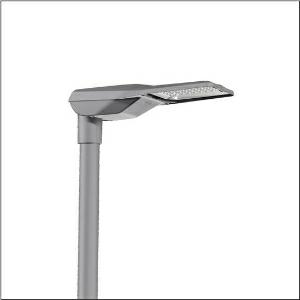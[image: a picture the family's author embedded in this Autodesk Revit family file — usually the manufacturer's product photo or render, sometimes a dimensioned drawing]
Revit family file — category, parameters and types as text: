
# Revit family: streetlight_sl_21_iq_mini___st0_5a_5xe2b31g08jb_3c5a
name_source: partatom
category: Lighting Fixtures
units: mm (PartAtom-declared; Revit-internal decimal feet)

## family parameters
Cut with Voids When Loaded = No
Host = Face
Light Source = No
Part Type = Normal
Room Calculation Point = No
Round Connector Dimension = Use Diameter
Shared = No

## types (1)
- --- (1 x LED, 10820 lm, 71.6 W, 3000K)
    Apparent Load = 72 VA
    CIE Flux Codes = 43 76 97 100 100
    Color Rendering = 70
    Color Temperature = 3000K
    Default Elevation = 1800 mm
    Description = Streetlight SL 21 mini, mast luminaire, primary light control with lens, of PMMA, primary optical cover: cover, of toughened safety glass, transparent, light distribution: ST0.5a, light emission: direct distribution, primary light characteristic: asymmetric, installation type: post-top, side-entry, LED, High Power LED, rated luminous flux: 10.820lm, luminous efficacy: 151lm/W, light colour: 730, colour temperature: 3000K, control gear: ECG iQ, control: Street-Remote, Auto-Match, Temp-Guard, Lumen-Switch, Night-Set, Smart-Wire, Light-Fading, Desk-Remote (wireless, voltage-free reading and setting of iQ features in the workshop via application-optimized NFC function/RFID function), optimised constant luminous flux control (CLO 2.0), mains connection: 220..240V, AC, 50/60Hz, start of lifetime: 72W, end of lifetime: 75W, reduction: 33W, luminaire housing, of diecast aluminium, powder-coated, Siteco® metallic grey (DB 702S), corrosivity category C5 according to DIN EN ISO 12944, length: 628mm, width: 235mm, height: 110mm, spigot size: 60/76mm (post-top) and 42/60/76mm (side-entry), mast flange for spigot size: 42mm: 5XC10008XM4, 60mm: 5XC10008XM2, 76/60mm: 5XC10108XM1, protection rating (complete): IP66, insulation class (complete): insulation class II (safety insulation), certification: CE, ENEC, VDE, impact resistance: IK09, permissible operating ambient temperature for outdoor applications: -40..+50°C, standard-compliant lighting for roads and squares, packaging unit: 1 piece

Light Distribution: ST0.5a
    Height = 110 mm
    Lamp = 1 x LED
    Lamp Light Flux = 10820 lm
    Lamp Power = 71.6 W
    Lamp count = 1
    Length = 625 mm
    Luminous efficacy = 151 lm/W
    Manufacturer = Siteco
    ModVariant = No
    Model = 5XE2B31G08JB
    Number of Poles = 1
    OnlyDefault = Yes
    Power Factor = 1
    Product Name = Streetlight SL 21 iQ mini | ST0.5a
    Product group = mast luminaire | pylon top
    ProductGroupID = 6100
    Protection Class = Protection class II
    Protection Degree = IP 66
    RLX_Detail_Level = 1
    RlxData = <blob elided: 103413 chars, md5=2ec15231>
    Socket = socket
    Standby Power = 0 W
    System Light Flux = 10820 lm
    System Power = 72 W
    Type Comments = factory setting: luminous flux: 100 % | dim-lin: 254 | 746 mA
    Type Image = l_1003519.jpg
    URL = http://relux.com
    VarID = @adj_084171
    Voltage = 0 V
    Weight = 0.00 kg
    Width = 234 mm

## geometry (parser evidence)
native form markers: Blend x4, Sweep x12
no freeform markers — native parametric forms only
